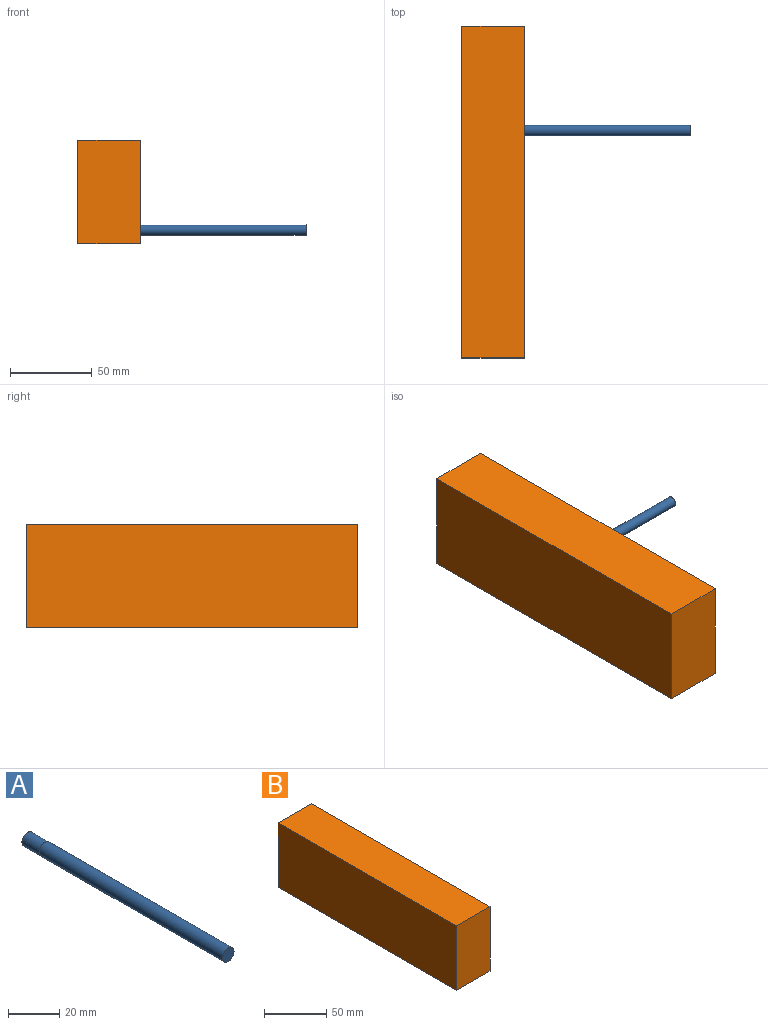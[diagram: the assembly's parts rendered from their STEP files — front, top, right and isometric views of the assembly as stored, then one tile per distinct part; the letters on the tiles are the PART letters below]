
ASSEMBLY  parts=2 mates=1
PART A: 5 faces, bbox 6.4x111.1x6.4 mm
  f0: cylinder r=3.11mm len=9.53mm, axis (0,-1,0), area 186.2mm2, adj f1,f4
  f1: plane 6.22x6.22mm, normal (0,1,0), area 30.4mm2, adj f0
  f2: cylinder r=3.17mm len=101.6mm, axis (0,1,0), area 2026.8mm2, adj f3,f4
  f3: plane 6.35x6.35mm, normal (0,-1,0), area 31.7mm2, adj f2
  f4: plane 6.35x6.35mm, normal (0,1,0), area 1.3mm2, adj f0,f2
PART B: 8 faces, bbox 38.1x203.2x63.5 mm
  f0: plane 63.5x38.1mm, normal (0,-1,0), area 2419.3mm2, adj f1,f3,f4,f5
  f1: plane 203.2x38.1mm, normal (0,0,-1), area 7741.9mm2, adj f0,f2,f4,f5
  f2: plane 63.5x38.1mm, normal (0,1,0), area 2419.3mm2, adj f1,f3,f4,f5
  f3: plane 203.2x38.1mm, normal (0,0,1), area 7741.9mm2, adj f0,f2,f4,f5
  f4: plane 203.2x63.5mm, normal (1,0,0), area 12885.4mm2, adj f0,f1,f2,f3,f6
  f5: plane 203.2x63.5mm, normal (-1,0,0), area 12903.2mm2, adj f0,f1,f2,f3
  f6: cylinder r=2.38mm len=12.7mm, axis (1,0,0), area 190mm2, adj f4,f7
  f7: plane 4.76x4.76mm, normal (1,0,0), area 17.8mm2, adj f6
PLACE A rot(axis=(-0.58,0.58,0.58),120deg) t=(18.58,32.01,-10.6)mm
PLACE B t=(-0.47,1.98,3.37)mm fixed
MATE fastened A.f0 <-> B.f6  axis (-1,0,0) through (18.58,32.01,-10.6)mm
